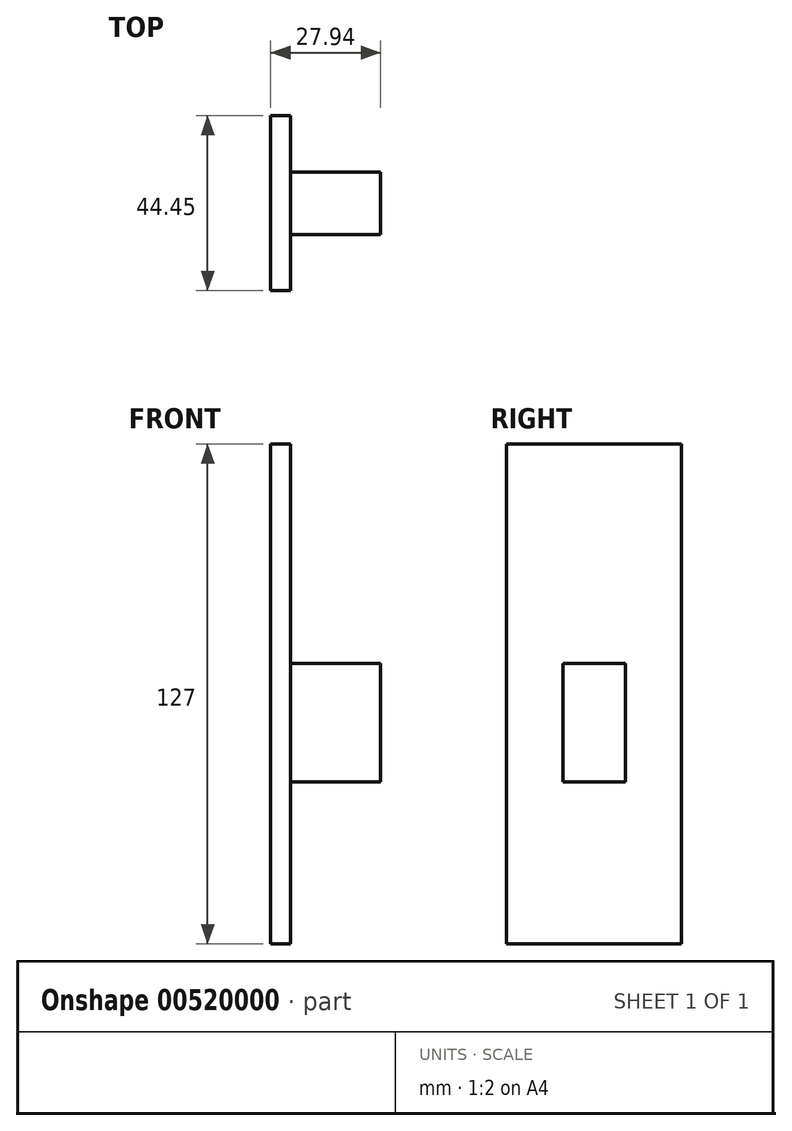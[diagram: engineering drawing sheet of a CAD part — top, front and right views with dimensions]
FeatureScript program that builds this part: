
annotation { "Feature Type Name" : "Feature", "Feature Type Description" : "" }
export const myFeature = defineFeature(function(context is Context, id is Id, definition is map)
    precondition{}
    {
        {
            var Q0;
            Q0=qCreatedBy(makeId("Right.planeOp"),FACE);
            var sketch = newSketch(context, id + "F0", { "sketchPlane" : qUnion([Q0])});
            skLineSegment(sketch, "E0", {"start": v(0, 0) * mm, "end": v(0, 127) * mm});
            skLineSegment(sketch, "E1", {"start": v(0, 127) * mm, "end": v(44.45, 127) * mm});
            skLineSegment(sketch, "E2", {"start": v(44.45, 127) * mm, "end": v(44.45, 0) * mm});
            skLineSegment(sketch, "E3", {"start": v(44.45, 0) * mm, "end": v(0, 0) * mm});
            skSolve(sketch);
        }
        {
            var Q0;
            Q0=makeQuery(id+"F0.imprint","IMPRINT",FACE,{"disambiguationData":[TD([[makeQuery(id+"F0.imprint","IMPRINT",EDGE,{"derivedFrom":sQuery(id+"F0.wireOp",EDGE,"E0")}),-1.0]])]});
            var sketch = newSketch(context, id + "F1", { "sketchPlane" : qUnion([Q0])});
            skSolve(sketch);
        }
        {
            var Q0;
            Q0 = qSketchRegion(id + "F1", true);
            var Q1;
            Q1=makeQuery(id+"F0.imprint","IMPRINT",FACE,{"disambiguationData":[TD([[makeQuery(id+"F0.imprint","IMPRINT",EDGE,{"derivedFrom":sQuery(id+"F0.wireOp",EDGE,"E0")}),-1.0]])]});
            extrude(context, id + "F2", {"entities" : qUnion([Q0, Q1]), "depth" : 5.08 * mm, "offsetDistance" : 25.4 * mm});
        }
        {
            var Q0;
            Q0=makeQuery(id+"F2.opExtrude","CAP_FACE",FACE,{"disambiguationData":[OSD([sQuery(id+"F0.wireOp",EDGE,"E0"),sQuery(id+"F0.wireOp",EDGE,"E1"),sQuery(id+"F0.wireOp",EDGE,"E2"),sQuery(id+"F0.wireOp",EDGE,"E3")])],"isStart":false});
            var sketch = newSketch(context, id + "F3", { "sketchPlane" : qUnion([Q0])});
            skLineSegment(sketch, "E4.bottom", {"start": v(30.16, 41.13) * mm, "end": v(14.29, 41.13) * mm});
            skLineSegment(sketch, "E4.top", {"start": v(30.16, 71.3) * mm, "end": v(14.29, 71.3) * mm});
            skLineSegment(sketch, "E4.left", {"start": v(30.16, 41.13) * mm, "end": v(30.16, 71.3) * mm});
            skLineSegment(sketch, "E4.right", {"start": v(14.29, 41.13) * mm, "end": v(14.29, 71.3) * mm});
            skPoint(sketch, "E4.middle", {"position": v(22.23, 56.21) * mm});
            skLineSegment(sketch, "E5", {"start": v(22.22, 127) * mm, "end": v(22.23, 56.21) * mm, "construction": true});
            skSolve(sketch);
        }
        {
            var Q0;
            Q0=makeQuery(id+"F3.imprint","IMPRINT",FACE,{"disambiguationData":[TD([[makeQuery(id+"F3.imprint","IMPRINT",EDGE,{"derivedFrom":sQuery(id+"F3.wireOp",EDGE,"E4.bottom")}),-1.0]])]});
            extrude(context, id + "F4", {"entities" : qUnion([Q0]), "operationType" : NewBodyOperationType.ADD, "depth" : 22.86 * mm, "offsetDistance" : 25.4 * mm});
        }
    });
